# Revit family: ROSENBERG_Z_R
name_source: partatom
category: Wyposażenie mechaniczne
revit_build: Autodesk Revit MEP 2016 (Build: 20150220_1215(x64)
units: mm (PartAtom-declared; Revit-internal decimal feet)

## family parameters
Numer OmniClass = 23.75.00.00
Oparty na płaszczyźnie roboczej = Nie
Punkt obliczania pomieszczeń = Nie
Tnij formami wycięć po wczytaniu = Nie
Typ części = Dzieli na
Tytuł OmniClass = Climate Control (HVAC)
Współdzielony = Tak
Wymiar okrągłego złącza = Użyj średnicy
Zawsze pionowo = Tak

## types (7) — shared parameters
Charakterystyka pracy = https://rosenberg.pl
Częstotliwość = 50 Hz
Klasa szczelności = IP44
Materiał = <Wg kategorii>
Napięcie znamionowe = 230 V
Opis = Wentylator kanałowy Zerobox Revolution
Producent = Rosenberg
URL = https://rosenberg.pl
param_Sr.wenty = 122 mm  [stored 0.400262 ft]
param_Wysokość kołnierza = 30 mm  [stored 0.0984252 ft]

## per-type parameters (varying)
| type | Masa | Moc znamionowa | Numer katalogowy | Prąd znamionowy | param_Skrzynia długość | param_Went.Przył.odsunięcie X | param_Went.Przył.odsunięcie Y | param_Wentylator długość | param_Wentylator szerokość | param_Wentylator wysokość | param_b1 | param_f1 | param_wymiar otworowanie | Średnica przyłącza |
| Z 250.3EF R1 | 19.50 kg | 200 W | F05-25012 | 1 A | 420 mm | 233 mm | 175 mm  [stored 0.574147 ft] | 520 mm | 465 mm | 355 mm | 130 mm | 347 mm | 244 mm | 250 mm  [stored 0.82021 ft] |
| Z 200.3DF R1 | 17.50 kg | 124 W | F05-20012 | 1 A | 390 mm | 210 mm | 165 mm | 490 mm | 420 mm | 315 mm | 123 mm | 327 mm | 194 mm | 200 mm  [stored 0.656168 ft] |
| Z 160.3CF R1 | 14.50 kg | 100 W | F05-16012 | 0 A | 360 mm | 190 mm | 140 mm | 460 mm | 380 mm | 265 mm | 115 mm | 307 mm | 154 mm | 160 mm |
| Z 125.2CA R1 | 13.00 kg | 29 W | F05-12512 | 0 A | 360 mm | 190 mm | 140 mm | 460 mm | 380 mm | 245 mm | 115 mm | 307 mm | 119 mm | 125 mm  [stored 0.410105 ft] |
| Z 400.5FA R1 | 44.00 kg | 290 W | F05-40009 | 1 A | 650 mm | 323 mm | 228 mm | 750 mm | 645 mm | 470 mm | 188 mm | 500 mm | 394 mm | 400 mm |
| Z 355.5FA R1 | 44.00 kg | 290 W | F05-35513 | 1 A | 600 mm | 310 mm | 230 mm | 700 mm | 620 mm | 460 mm | 175 mm  [stored 0.574147 ft] | 467 mm | 349 mm | 355 mm |
| Z 315.4EC R1 | 44.00 kg | 143 W | F05-31512 | 1 A | 580 mm | 298 mm | 212 mm | 680 mm | 595 mm | 420 mm | 170 mm | 453 mm | 309 mm | 315 mm |

note: column(s) folded — value = type name in every type: Model

note: [stored X ft] marks values corroborated as IEEE doubles in the binary element streams (Revit-internal decimal feet)

## geometry (parser evidence)
native form markers: Blend x2, Sweep x3
no freeform markers — native parametric forms only
